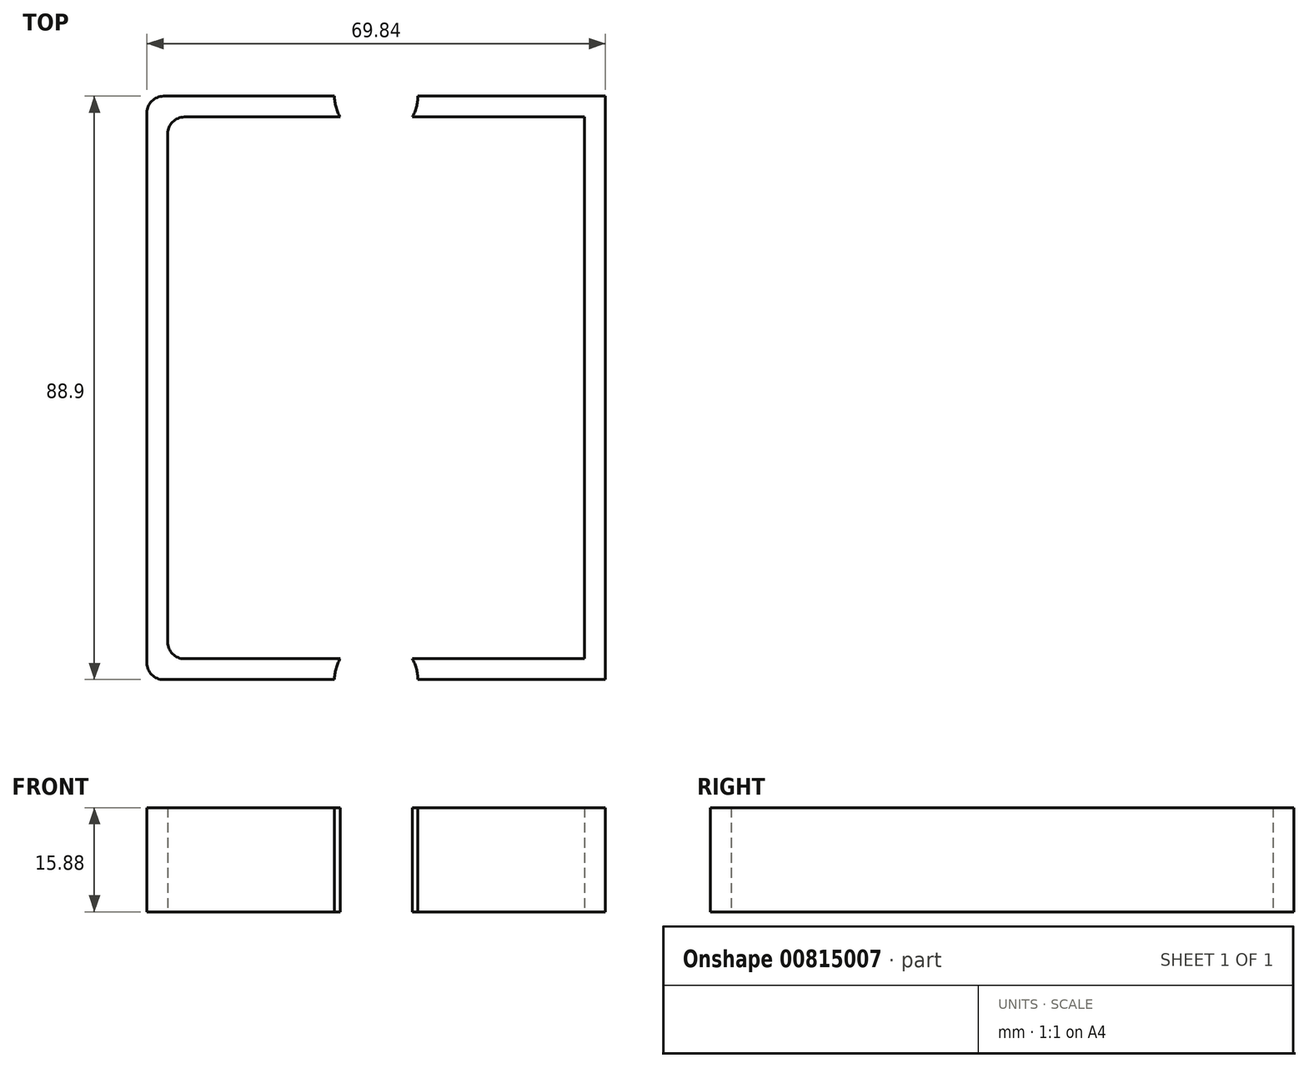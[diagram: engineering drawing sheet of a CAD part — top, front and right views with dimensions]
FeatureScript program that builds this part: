
annotation { "Feature Type Name" : "Feature", "Feature Type Description" : "" }
export const myFeature = defineFeature(function(context is Context, id is Id, definition is map)
    precondition{}
    {
        {
            var Q0;
            Q0=qCreatedBy(makeId("Top.planeOp"),FACE);
            var sketch = newSketch(context, id + "F0", { "sketchPlane" : qUnion([Q0])});
            skLineSegment(sketch, "E0.bottom", {"start": v(-31.75, 41.28) * mm, "end": v(31.75, 41.28) * mm});
            skLineSegment(sketch, "E0.top", {"start": v(-31.75, -41.28) * mm, "end": v(31.75, -41.28) * mm});
            skLineSegment(sketch, "E0.left", {"start": v(-31.75, 41.28) * mm, "end": v(-31.75, -41.28) * mm});
            skLineSegment(sketch, "E0.right", {"start": v(31.75, 41.28) * mm, "end": v(31.75, -41.28) * mm});
            skPoint(sketch, "E0.middle", {"position": v(0, 0) * mm});
            skLineSegment(sketch, "E1.bottom", {"start": v(-34.92, 44.45) * mm, "end": v(34.93, 44.45) * mm});
            skLineSegment(sketch, "E1.top", {"start": v(-34.93, -44.45) * mm, "end": v(34.92, -44.45) * mm});
            skLineSegment(sketch, "E1.left", {"start": v(-34.92, 44.45) * mm, "end": v(-34.93, -44.45) * mm});
            skLineSegment(sketch, "E1.right", {"start": v(34.93, 44.45) * mm, "end": v(34.92, -44.45) * mm});
            skCircle(sketch, "E2", {"center": v(0, 44.45) * mm, "radius": 6.35 * mm});
            skCircle(sketch, "E3", {"center": v(-34.92, 44.45) * mm, "radius": 6.35 * mm});
            skCircle(sketch, "E4", {"center": v(-34.93, -44.45) * mm, "radius": 6.35 * mm});
            skCircle(sketch, "E5", {"center": v(0, -44.45) * mm, "radius": 6.35 * mm});
            skSolve(sketch);
        }
        {
            var Q0;
            {var subQ0=sQuery(id+"F0.wireOp",EDGE,"E1.left");var subQ1=sQuery(id+"F0.wireOp",EDGE,"E1.bottom");var subQ2=makeQuery(id+"F0.imprint","INTERSECT",VERTEX,{"derivedFrom":[subQ1,subQ0]});Q0=makeQuery(id+"F0.imprint","IMPRINT",FACE,{"disambiguationData":[TD([[makeQuery(id+"F0.imprint","IMPRINT",EDGE,{"disambiguationData":[TD([[subQ2,-1.0]])],"derivedFrom":subQ1}),1.0]])]});}
            var Q1;
            {var subQ0=sQuery(id+"F0.wireOp",EDGE,"E2");var subQ1=sQuery(id+"F0.wireOp",EDGE,"E1.bottom");var subQ2=makeQuery(id+"F0.imprint","INTERSECT",VERTEX,{"disambiguationData":[OD(0.0)],"derivedFrom":[subQ1,subQ0]});Q1=makeQuery(id+"F0.imprint","IMPRINT",FACE,{"disambiguationData":[TD([[makeQuery(id+"F0.imprint","IMPRINT",EDGE,{"disambiguationData":[TD([[subQ2,-1.0]])],"derivedFrom":subQ1}),1.0]])]});}
            var Q2;
            {var subQ0=sQuery(id+"F0.wireOp",EDGE,"E1.left");var subQ1=sQuery(id+"F0.wireOp",EDGE,"E1.top");var subQ2=makeQuery(id+"F0.imprint","INTERSECT",VERTEX,{"derivedFrom":[subQ1,subQ0]});Q2=makeQuery(id+"F0.imprint","IMPRINT",FACE,{"disambiguationData":[TD([[makeQuery(id+"F0.imprint","IMPRINT",EDGE,{"disambiguationData":[TD([[subQ2,-1.0]])],"derivedFrom":subQ1}),-1.0]])]});}
            var Q3;
            {var subQ0=sQuery(id+"F0.wireOp",EDGE,"E5");var subQ1=sQuery(id+"F0.wireOp",EDGE,"E1.top");var subQ2=makeQuery(id+"F0.imprint","INTERSECT",VERTEX,{"disambiguationData":[OD(0.0)],"derivedFrom":[subQ1,subQ0]});Q3=makeQuery(id+"F0.imprint","IMPRINT",FACE,{"disambiguationData":[TD([[makeQuery(id+"F0.imprint","IMPRINT",EDGE,{"disambiguationData":[TD([[subQ2,-1.0]])],"derivedFrom":subQ1}),-1.0]])]});}
            var Q4;
            {var subQ0=sQuery(id+"F0.wireOp",EDGE,"E3");var subQ1=sQuery(id+"F0.wireOp",EDGE,"E0.bottom");var subQ2=makeQuery(id+"F0.imprint","INTERSECT",VERTEX,{"derivedFrom":[subQ1,subQ0]});Q4=makeQuery(id+"F0.imprint","IMPRINT",FACE,{"disambiguationData":[TD([[makeQuery(id+"F0.imprint","IMPRINT",EDGE,{"disambiguationData":[TD([[subQ2,-1.0]])],"derivedFrom":subQ1}),1.0]])]});}
            var Q5;
            {var subQ0=sQuery(id+"F0.wireOp",EDGE,"E4");var subQ1=sQuery(id+"F0.wireOp",EDGE,"E0.top");var subQ2=makeQuery(id+"F0.imprint","INTERSECT",VERTEX,{"derivedFrom":[subQ1,subQ0]});Q5=makeQuery(id+"F0.imprint","IMPRINT",FACE,{"disambiguationData":[TD([[makeQuery(id+"F0.imprint","IMPRINT",EDGE,{"disambiguationData":[TD([[subQ2,-1.0]])],"derivedFrom":subQ1}),-1.0]])]});}
            var Q6;
            {var subQ0=sQuery(id+"F0.wireOp",EDGE,"E3");var subQ1=sQuery(id+"F0.wireOp",EDGE,"E0.left");var subQ2=makeQuery(id+"F0.imprint","INTERSECT",VERTEX,{"derivedFrom":[subQ1,subQ0]});Q6=makeQuery(id+"F0.imprint","IMPRINT",FACE,{"disambiguationData":[TD([[makeQuery(id+"F0.imprint","IMPRINT",EDGE,{"disambiguationData":[TD([[subQ2,-1.0]])],"derivedFrom":subQ1}),-1.0]])]});}
            var Q7;
            {var subQ5=sQuery(id+"F0.wireOp",EDGE,"E0.left");var subQ6=sQuery(id+"F0.wireOp",EDGE,"E0.bottom");var subQ7=makeQuery(id+"F0.imprint","INTERSECT",VERTEX,{"derivedFrom":[subQ6,subQ5]});Q7=makeQuery(id+"F0.imprint","IMPRINT",FACE,{"disambiguationData":[TD([[makeQuery(id+"F0.imprint","IMPRINT",EDGE,{"disambiguationData":[TD([[subQ7,-1.0]])],"derivedFrom":subQ6}),1.0]])]});}
            var Q8;
            {var subQ0=sQuery(id+"F0.wireOp",EDGE,"E2");var subQ1=sQuery(id+"F0.wireOp",EDGE,"E0.bottom");var subQ2=makeQuery(id+"F0.imprint","INTERSECT",VERTEX,{"disambiguationData":[OD(0.0)],"derivedFrom":[subQ1,subQ0]});Q8=makeQuery(id+"F0.imprint","IMPRINT",FACE,{"disambiguationData":[TD([[makeQuery(id+"F0.imprint","IMPRINT",EDGE,{"disambiguationData":[TD([[subQ2,-1.0]])],"derivedFrom":subQ1}),1.0]])]});}
            var Q9;
            {var subQ6=sQuery(id+"F0.wireOp",EDGE,"E0.left");var subQ7=sQuery(id+"F0.wireOp",EDGE,"E0.top");var subQ8=makeQuery(id+"F0.imprint","INTERSECT",VERTEX,{"derivedFrom":[subQ7,subQ6]});Q9=makeQuery(id+"F0.imprint","IMPRINT",FACE,{"disambiguationData":[TD([[makeQuery(id+"F0.imprint","IMPRINT",EDGE,{"disambiguationData":[TD([[subQ8,-1.0]])],"derivedFrom":subQ7}),-1.0]])]});}
            var Q10;
            {var subQ0=sQuery(id+"F0.wireOp",EDGE,"E5");var subQ1=sQuery(id+"F0.wireOp",EDGE,"E0.top");var subQ2=makeQuery(id+"F0.imprint","INTERSECT",VERTEX,{"disambiguationData":[OD(0.0)],"derivedFrom":[subQ1,subQ0]});Q10=makeQuery(id+"F0.imprint","IMPRINT",FACE,{"disambiguationData":[TD([[makeQuery(id+"F0.imprint","IMPRINT",EDGE,{"disambiguationData":[TD([[subQ2,-1.0]])],"derivedFrom":subQ1}),-1.0]])]});}
            extrude(context, id + "F1", {"entities" : qUnion([Q0, Q1, Q2, Q3, Q4, Q5, Q6, Q7, Q8, Q9, Q10]), "depth" : 3.17 * mm, "offsetDistance" : 25.4 * mm});
        }
        {
            var Q0;
            {var subQ0=sQuery(id+"F0.wireOp",EDGE,"E3");var subQ1=sQuery(id+"F0.wireOp",EDGE,"E0.bottom");var subQ2=makeQuery(id+"F0.imprint","INTERSECT",VERTEX,{"derivedFrom":[subQ1,subQ0]});Q0=makeQuery(id+"F0.imprint","IMPRINT",FACE,{"disambiguationData":[TD([[makeQuery(id+"F0.imprint","IMPRINT",EDGE,{"disambiguationData":[TD([[subQ2,-1.0]])],"derivedFrom":subQ1}),1.0]])]});}
            var Q1;
            {var subQ0=sQuery(id+"F0.wireOp",EDGE,"E2");var subQ1=sQuery(id+"F0.wireOp",EDGE,"E0.bottom");var subQ2=makeQuery(id+"F0.imprint","INTERSECT",VERTEX,{"disambiguationData":[OD(0.0)],"derivedFrom":[subQ1,subQ0]});Q1=makeQuery(id+"F0.imprint","IMPRINT",FACE,{"disambiguationData":[TD([[makeQuery(id+"F0.imprint","IMPRINT",EDGE,{"disambiguationData":[TD([[subQ2,-1.0]])],"derivedFrom":subQ1}),1.0]])]});}
            var Q2;
            {var subQ5=sQuery(id+"F0.wireOp",EDGE,"E0.left");var subQ6=sQuery(id+"F0.wireOp",EDGE,"E0.bottom");var subQ7=makeQuery(id+"F0.imprint","INTERSECT",VERTEX,{"derivedFrom":[subQ6,subQ5]});Q2=makeQuery(id+"F0.imprint","IMPRINT",FACE,{"disambiguationData":[TD([[makeQuery(id+"F0.imprint","IMPRINT",EDGE,{"disambiguationData":[TD([[subQ7,-1.0]])],"derivedFrom":subQ6}),1.0]])]});}
            var Q3;
            {var subQ0=sQuery(id+"F0.wireOp",EDGE,"E3");var subQ1=sQuery(id+"F0.wireOp",EDGE,"E0.left");var subQ2=makeQuery(id+"F0.imprint","INTERSECT",VERTEX,{"derivedFrom":[subQ1,subQ0]});Q3=makeQuery(id+"F0.imprint","IMPRINT",FACE,{"disambiguationData":[TD([[makeQuery(id+"F0.imprint","IMPRINT",EDGE,{"disambiguationData":[TD([[subQ2,-1.0]])],"derivedFrom":subQ1}),-1.0]])]});}
            var Q4;
            {var subQ6=sQuery(id+"F0.wireOp",EDGE,"E0.left");var subQ7=sQuery(id+"F0.wireOp",EDGE,"E0.top");var subQ8=makeQuery(id+"F0.imprint","INTERSECT",VERTEX,{"derivedFrom":[subQ7,subQ6]});Q4=makeQuery(id+"F0.imprint","IMPRINT",FACE,{"disambiguationData":[TD([[makeQuery(id+"F0.imprint","IMPRINT",EDGE,{"disambiguationData":[TD([[subQ8,-1.0]])],"derivedFrom":subQ7}),-1.0]])]});}
            var Q5;
            {var subQ0=sQuery(id+"F0.wireOp",EDGE,"E4");var subQ1=sQuery(id+"F0.wireOp",EDGE,"E0.top");var subQ2=makeQuery(id+"F0.imprint","INTERSECT",VERTEX,{"derivedFrom":[subQ1,subQ0]});Q5=makeQuery(id+"F0.imprint","IMPRINT",FACE,{"disambiguationData":[TD([[makeQuery(id+"F0.imprint","IMPRINT",EDGE,{"disambiguationData":[TD([[subQ2,-1.0]])],"derivedFrom":subQ1}),-1.0]])]});}
            var Q6;
            {var subQ0=sQuery(id+"F0.wireOp",EDGE,"E5");var subQ1=sQuery(id+"F0.wireOp",EDGE,"E0.top");var subQ2=makeQuery(id+"F0.imprint","INTERSECT",VERTEX,{"disambiguationData":[OD(0.0)],"derivedFrom":[subQ1,subQ0]});Q6=makeQuery(id+"F0.imprint","IMPRINT",FACE,{"disambiguationData":[TD([[makeQuery(id+"F0.imprint","IMPRINT",EDGE,{"disambiguationData":[TD([[subQ2,-1.0]])],"derivedFrom":subQ1}),-1.0]])]});}
            extrude(context, id + "F2", {"entities" : qUnion([Q0, Q1, Q2, Q3, Q4, Q5, Q6]), "operationType" : NewBodyOperationType.ADD, "depth" : 19.05 * mm, "offsetDistance" : 25.4 * mm});
        }
        {
            var Q0;
            {var subQ4=sQuery(id+"F0.wireOp",EDGE,"E0.right");Q0=makeQuery(id+"F0.imprint","IMPRINT",FACE,{"disambiguationData":[TD([[makeQuery(id+"F0.imprint","IMPRINT",EDGE,{"derivedFrom":subQ4}),1.0]])]});}
            var Q1;
            {var subQ0=sQuery(id+"F0.wireOp",EDGE,"E0.right");Q1=makeQuery(id+"F0.imprint","IMPRINT",FACE,{"disambiguationData":[TD([[makeQuery(id+"F0.imprint","IMPRINT",EDGE,{"derivedFrom":subQ0}),-1.0]])]});}
            var Q2;
            {var subQ0=sQuery(id+"F0.wireOp",EDGE,"E2");var subQ1=sQuery(id+"F0.wireOp",EDGE,"E0.bottom");var subQ2=makeQuery(id+"F0.imprint","INTERSECT",VERTEX,{"disambiguationData":[OD(0.0)],"derivedFrom":[subQ1,subQ0]});Q2=makeQuery(id+"F0.imprint","IMPRINT",FACE,{"disambiguationData":[TD([[makeQuery(id+"F0.imprint","IMPRINT",EDGE,{"disambiguationData":[TD([[subQ2,-1.0]])],"derivedFrom":subQ1}),-1.0]])]});}
            var Q3;
            {var subQ0=sQuery(id+"F0.wireOp",EDGE,"E0.left");var subQ1=sQuery(id+"F0.wireOp",EDGE,"E0.bottom");var subQ2=makeQuery(id+"F0.imprint","INTERSECT",VERTEX,{"derivedFrom":[subQ1,subQ0]});Q3=makeQuery(id+"F0.imprint","IMPRINT",FACE,{"disambiguationData":[TD([[makeQuery(id+"F0.imprint","IMPRINT",EDGE,{"disambiguationData":[TD([[subQ2,-1.0]])],"derivedFrom":subQ1}),-1.0]])]});}
            var Q4;
            {var subQ0=sQuery(id+"F0.wireOp",EDGE,"E5");var subQ1=sQuery(id+"F0.wireOp",EDGE,"E0.top");var subQ2=makeQuery(id+"F0.imprint","INTERSECT",VERTEX,{"disambiguationData":[OD(0.0)],"derivedFrom":[subQ1,subQ0]});Q4=makeQuery(id+"F0.imprint","IMPRINT",FACE,{"disambiguationData":[TD([[makeQuery(id+"F0.imprint","IMPRINT",EDGE,{"disambiguationData":[TD([[subQ2,-1.0]])],"derivedFrom":subQ1}),1.0]])]});}
            var Q5;
            {var subQ0=sQuery(id+"F0.wireOp",EDGE,"E0.left");var subQ1=sQuery(id+"F0.wireOp",EDGE,"E0.top");var subQ2=makeQuery(id+"F0.imprint","INTERSECT",VERTEX,{"derivedFrom":[subQ1,subQ0]});Q5=makeQuery(id+"F0.imprint","IMPRINT",FACE,{"disambiguationData":[TD([[makeQuery(id+"F0.imprint","IMPRINT",EDGE,{"disambiguationData":[TD([[subQ2,-1.0]])],"derivedFrom":subQ1}),1.0]])]});}
            extrude(context, id + "F3", {"entities" : qUnion([Q0, Q1, Q2, Q3, Q4, Q5]), "operationType" : NewBodyOperationType.ADD, "depth" : 3.17 * mm, "offsetDistance" : 25.4 * mm});
        }
        {
            var Q0;
            Q0=makeQuery(id+"F3.opExtrude","CAP_EDGE",EDGE,{"disambiguationData":[OSD([sQuery(id+"F0.wireOp",EDGE,"E5")])],"isStart":false});
            var Q1;
            Q1=makeQuery(id+"F3.opExtrude","CAP_EDGE",EDGE,{"disambiguationData":[OSD([sQuery(id+"F0.wireOp",EDGE,"E2")])],"isStart":false});
            chamfer(context, id + "F4", {"entities" : qUnion([Q0, Q1]), "chamferType" : ChamferType.OFFSET_ANGLE, "width" : 17.78 * mm, "oppositeDirection" : false, "angle" : 50 * degree, "tangentPropagation" : true});
        }
        {
            var Q0;
            {var subQ0=sQuery(id+"F0.wireOp",EDGE,"E0.left");var subQ1=sQuery(id+"F0.wireOp",EDGE,"E0.bottom");Q0=makeQuery(id+"F2.boolean.opBoolean","MERGE",EDGE,{"derivedFrom":[makeQuery(id+"F1.opExtrude","SWEPT_EDGE",EDGE,{"disambiguationData":[OSD([subQ1,subQ0])]}),makeQuery(id+"F2.opExtrude","SWEPT_EDGE",EDGE,{"disambiguationData":[OSD([subQ1,subQ0])]})]});}
            var Q1;
            {var subQ0=sQuery(id+"F0.wireOp",EDGE,"E0.left");var subQ1=sQuery(id+"F0.wireOp",EDGE,"E0.top");Q1=makeQuery(id+"F2.boolean.opBoolean","MERGE",EDGE,{"derivedFrom":[makeQuery(id+"F1.opExtrude","SWEPT_EDGE",EDGE,{"disambiguationData":[OSD([subQ1,subQ0])]}),makeQuery(id+"F2.opExtrude","SWEPT_EDGE",EDGE,{"disambiguationData":[OSD([subQ1,subQ0])]})]});}
            var Q2;
            Q2=makeQuery(id+"F2.opExtrude","SWEPT_EDGE",EDGE,{"disambiguationData":[OSD([sQuery(id+"F0.wireOp",EDGE,"E1.top"),sQuery(id+"F0.wireOp",EDGE,"E1.left")])]});
            var Q3;
            Q3=makeQuery(id+"F2.opExtrude","SWEPT_EDGE",EDGE,{"disambiguationData":[OSD([sQuery(id+"F0.wireOp",EDGE,"E1.bottom"),sQuery(id+"F0.wireOp",EDGE,"E1.left")])]});
            fillet(context, id + "F5", {"entities" : qUnion([Q0, Q1, Q2, Q3]), "radius" : 2.54 * mm, "tangentPropagation" : true, "allowEdgeOverflow" : false});
        }
        {
            var Q0;
            Q0=qCreatedBy(makeId("Top.planeOp"),FACE);
            var sketch = newSketch(context, id + "F6", { "sketchPlane" : qUnion([Q0])});
            skLineSegment(sketch, "E6.bottom", {"start": v(-96.85, -119.65) * mm, "end": v(76.6, -119.65) * mm});
            skLineSegment(sketch, "E6.top", {"start": v(-96.85, 195.55) * mm, "end": v(76.6, 195.55) * mm});
            skLineSegment(sketch, "E6.left", {"start": v(-96.85, -119.65) * mm, "end": v(-96.85, 195.55) * mm});
            skLineSegment(sketch, "E6.right", {"start": v(76.6, -119.65) * mm, "end": v(76.6, 195.55) * mm});
            skSolve(sketch);
        }
        {
            var Q0;
            Q0 = qSketchRegion(id + "F6", true);
            extrude(context, id + "F7", {"entities" : qUnion([Q0]), "operationType" : NewBodyOperationType.REMOVE, "depth" : 3.17 * mm, "offsetDistance" : 25.4 * mm});
        }
    });
